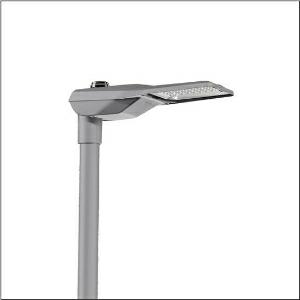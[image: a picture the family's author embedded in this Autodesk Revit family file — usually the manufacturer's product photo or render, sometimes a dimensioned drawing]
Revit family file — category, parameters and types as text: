
# Revit family: streetlight_sl_21_mini___stw1_0a_5xe6e37n08gb_9d35
name_source: partatom
category: Lighting Fixtures
units: mm (PartAtom-declared; Revit-internal decimal feet)

## family parameters
Cut with Voids When Loaded = No
Host = Face
Light Source = No
Part Type = Normal
Room Calculation Point = No
Round Connector Dimension = Use Diameter
Shared = No

## types (1)
- --- (1 x LED, 5940 lm, 40.4 W, 3000K)
    Apparent Load = 40 VA
    CIE Flux Codes = 38 75 98 100 100
    Color Rendering = 70
    Color Temperature = 3000K
    Default Elevation = 1800 mm
    Description = Streetlight SL 21 mini, mast luminaire, primary light control with lens, of PMMA, primary optical cover: cover, of toughened safety glass, transparent, light distribution: STW1.0a, light emission: direct distribution, primary light characteristic: asymmetric, installation type: side-entry, LED, 3G 1.5mm², High Power LED, rated luminous flux: 5.940lm, luminous efficacy: 147lm/W, light colour: 730, colour temperature: 3000K, control gear: NEMA (7pin), control: overheat protection, pre-setting: linear dimming characteristic, constant luminous flux control, time-dependent luminous flux control, flexible luminous flux parameterisation, mains connection: 230..240V, AC, 50/60Hz, connection cable pre-assembled, cable length: 8,5m, wiring characteristics: H07RN-F, start of lifetime: 40W, end of service life: 41W, reduction: 19W, luminaire housing, of diecast aluminium (EN AC-44300), powder-coated, Siteco® metallic grey (DB 702S), corrosivity category C5 mid according to DIN EN ISO 12944, multi-level sealing system, sealing non-destructively replaceable, inclination adjustable: 0°, 5°, 10°, 15°, length: 628mm, width: 235mm, height: 110mm, spigot size: 42mm (side-entry), mounting height: 4..8m, protection rating (complete): IP66, insulation class (complete): insulation class I (protective earthing), certification: CE, ENEC, ENEC+, VDE, impact resistance: IK10, permissible operating ambient temperature for outdoor applications: -40..+50°C, standard-compliant lighting for roads and squares, packaging unit: 1 piece

Light Distribution: STW1.0a
    Height = 110 mm
    Lamp = 1 x LED
    Lamp Light Flux = 5940 lm
    Lamp Power = 40.4 W
    Lamp count = 1
    Length = 625 mm
    Luminous efficacy = 147 lm/W
    Manufacturer = Siteco
    ModVariant = No
    Model = 5XE6E37N08GB
    Number of Poles = 1
    OnlyDefault = Yes
    Power Factor = 1
    Product Name = Streetlight SL 21 mini | STW1.0a
    Product group = mast luminaire | pylon top
    ProductGroupID = 6100
    Protection Class = Protection class I
    Protection Degree = IP 66
    RLX_Detail_Level = 1
    RLX_Emergency_Light_Flux = 0 lm
    RLX_Emergency_Type = 0
    RLX_Emergency_Type_DB = No
    RlxData = <blob elided: 25857 chars, md5=6421f535>
    Socket = socket
    Standby Power = 0 W
    System Light Flux = 5940 lm
    System Power = 40 W
    Type Comments = factory setting: luminous flux: 100 % | dim-lin: 254 | 812 mA
    Type Image = l_1294379.jpg
    URL = http://relux.com
    VarID = @adj_135716
    Voltage = 0 V
    Weight = 0.00 kg
    Width = 234 mm

## geometry (parser evidence)
native form markers: Blend x4, Sweep x12
no freeform markers — native parametric forms only
